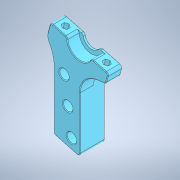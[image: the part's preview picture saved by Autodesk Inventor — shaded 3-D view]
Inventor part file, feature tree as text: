
AUTODESK INVENTOR PART (.ipt)
format: ipt  version: 2021.2 (Build 252289000, 289)  size: 375,296 bytes
history: native  units: mm
features: other x4, fillet x2, chamfer x2
ambient origin geometry x8: Origin, YZ Plane, XZ Plane, XY Plane, X Axis, Y Axis, Z Axis, Center Point
bodies: Body1 (feature_tree)
feature tree (8):
  other  "Твёрдое тело.ipt"
  fillet  "Сопряжение1"  Radius=10.0mm
  fillet  "Сопряжение2"  Radius=2.0mm
  chamfer  "Фаска1"  Distance=2.0mm
  chamfer  "Фаска2"  Distance=2.0mm Angle=45.0deg
  other  "Ножка правая верх::Твёрдое тело.ipt"
  other  "Элемент создания тегов1"
  other  "Твердое тело1"
